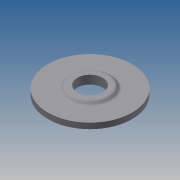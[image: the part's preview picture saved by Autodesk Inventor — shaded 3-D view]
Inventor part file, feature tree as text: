
AUTODESK INVENTOR PART (.ipt)
format: ipt  version: 2014 (Build 180170000, 170)  size: 100,352 bytes
history: native  units: mm
features: revolve x1, fillet x1, sketch x1
ambient origin geometry x8: Origin, YZ Plane, XZ Plane, XY Plane, X Axis, Y Axis, Z Axis, Center Point
bodies: Solid1 (feature_tree)
feature tree (3):
  revolve  "Revolution1"  [1 undecoded]
  fillet  "Fillet1"  Radius=6.5mm
  sketch  "Sketch1"  dims[d0=14.875mm d1=4.5mm d2=6.5mm d3=2.0mm d4=3.0mm d5=1.0mm d6=90.0deg d7=1.0mm]
note: 1 required parameter value undecoded (feature->parameter linkage not recoverable at this tier; creation-order binding heuristic only, values carry confidence <= 0.55)
